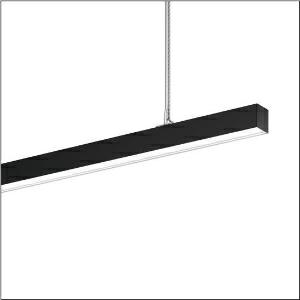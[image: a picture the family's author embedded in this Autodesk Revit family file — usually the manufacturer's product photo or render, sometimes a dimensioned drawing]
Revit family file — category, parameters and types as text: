
# Revit family: silica_21_51mx33db39bb
name_source: partatom
category: Lighting Fixtures
units: mm (PartAtom-declared; Revit-internal decimal feet)

## family parameters
Cut with Voids When Loaded = No
Host = Face
Light Source = No
Part Type = Normal
Room Calculation Point = No
Round Connector Dimension = Use Diameter
Shared = No

## types (1)
- --- (1 x LED, 7390 lm, 51.6 W, 3000K)
    Apparent Load = 52 VA
    CIE Flux Codes = 78 96 99 55 100
    Color Rendering = 80
    Color Temperature = 3000K
    Default Elevation = 1800 mm
    Description = Silica 21, office luminaire, primary optical cover: prismatic diffuser, of PMMA, CAT 2 (L<= 3000cd/m²), light emission: direct/indirect distribution, primary light characteristic: symmetric, installation type: suspended mounting, LED, rated luminous flux: 7.390lm, luminous efficacy: 143lm/W, light colour: 830, colour temperature: 3000K, control gear: DALI 2, with terminal, 3+2-pole, max. 2.5mm², mains connection: 220..240V, AC, 50/60Hz, rated input power: 51.6W, luminaire housing, of aluminium, matt jet black (RAL 9005), length: 1.504mm, width: 53mm, height: 53mm, protection rating (complete): IP20, insulation class (complete): insulation class I (protective earthing), certification: CE, permissible operating ambient temperature: 0..+35°C, standard: EN 50419, packaging unit: 1 piece
    Height = 53 mm
    Lamp = 1 x LED
    Lamp Light Flux = 7390 lm
    Lamp Power = 51.6 W
    Lamp count = 1
    Length = 1504 mm
    Luminous efficacy = 143 lm/W
    Manufacturer = Siteco
    ModVariant = No
    Model = 51MX33DB39BB
    Mounting Place = Ceiling
    Mounting Type = Pendant
    Number of Poles = 1
    OnlyDefault = Yes
    Power Factor = 1
    Product Name = Silica 21
    Product group = office luminaire | ceiling pendant
    ProductGroupID = 903
    Protection Class = Protection class I
    Protection Degree = IP 20
    RLX_Detail_Level = 1
    RLX_Emergency_Light_Flux = 0 lm
    RLX_Emergency_Type = 0
    RLX_Emergency_Type_DB = No
    RlxData = <blob elided: 26257 chars, md5=42316acb>
    Socket = socket
    Standby Power = 0 W
    System Light Flux = 7390 lm
    System Power = 52 W
    Type Comments = factory setting: luminous flux: 100 % | dim-lin: 254 | 345 mA
    Type Image = l_1335856.jpg
    URL = http://relux.com
    VarID = @adj_120101
    Voltage = 0 V
    Weight = 0.00 kg
    Width = 53 mm

## geometry (parser evidence)
native form markers: Blend x4, Sweep x17
no freeform markers — native parametric forms only
